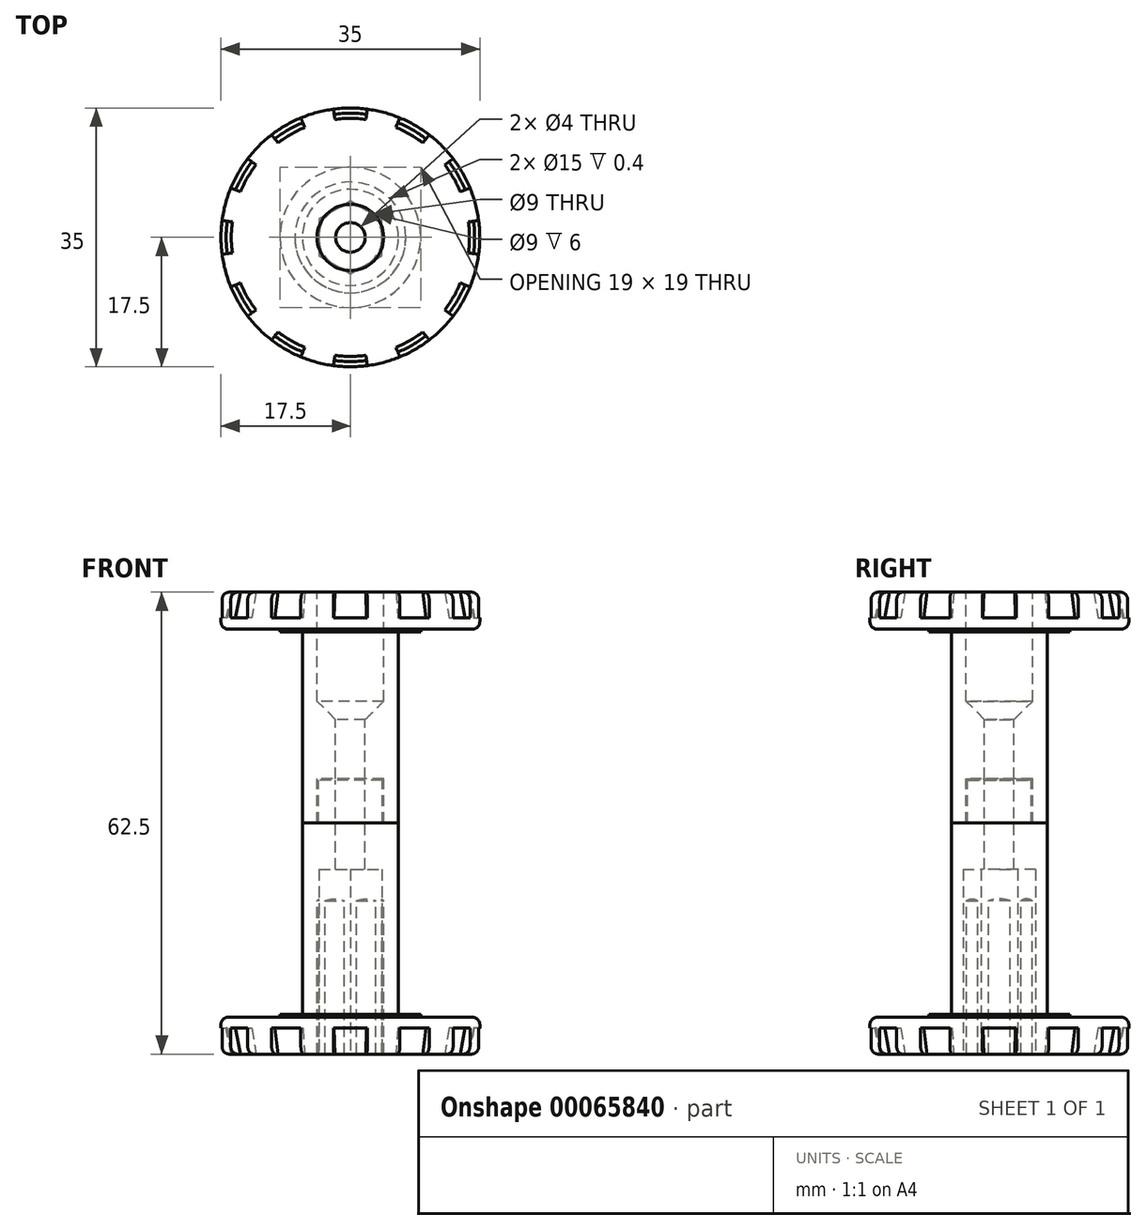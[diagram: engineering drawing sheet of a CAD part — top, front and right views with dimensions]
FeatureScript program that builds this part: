
annotation { "Feature Type Name" : "Feature", "Feature Type Description" : "" }
export const myFeature = defineFeature(function(context is Context, id is Id, definition is map)
    precondition{}
    {
        {
            var Q0;
            Q0=qCreatedBy(makeId("Front.planeOp"),FACE);
            var sketch = newSketch(context, id + "F0", { "sketchPlane" : qUnion([Q0])});
            skLineSegment(sketch, "E0", {"start": v(0, 0) * mm, "end": v(0, -45.3) * mm, "construction": true});
            skLineSegment(sketch, "E1.bottom", {"start": v(4.5, 0) * mm, "end": v(17.5, 0) * mm});
            skLineSegment(sketch, "E1.top", {"start": v(4.5, 62.5) * mm, "end": v(17.5, 62.5) * mm});
            skLineSegment(sketch, "E1.left", {"start": v(4.5, 0) * mm, "end": v(4.5, 62.5) * mm});
            skLineSegment(sketch, "E1.right", {"start": v(17.5, 0) * mm, "end": v(17.5, 62.5) * mm});
            skLineSegment(sketch, "E2", {"start": v(17.5, 5) * mm, "end": v(6.5, 5) * mm});
            skLineSegment(sketch, "E3", {"start": v(6.5, 5) * mm, "end": v(6.5, 31.25) * mm});
            skPoint(sketch, "E4", {"position": v(4.5, 31.25) * mm});
            skLineSegment(sketch, "E5", {"start": v(4.5, 31.25) * mm, "end": v(6.5, 31.25) * mm});
            skLineSegment(sketch, "E6", {"start": v(6.5, 31.25) * mm, "end": v(6.5, 57.5) * mm});
            skLineSegment(sketch, "E7", {"start": v(6.5, 57.5) * mm, "end": v(17.5, 57.5) * mm});
            skLineSegment(sketch, "E8", {"start": v(4.5, 20.75) * mm, "end": v(2, 23.25) * mm});
            skLineSegment(sketch, "E9", {"start": v(2, 23.25) * mm, "end": v(2, 37.25) * mm});
            skLineSegment(sketch, "E10", {"start": v(2, 37.25) * mm, "end": v(4.5, 37.25) * mm});
            skLineSegment(sketch, "E11", {"start": v(2, 37.25) * mm, "end": v(2, 45.25) * mm});
            skLineSegment(sketch, "E12", {"start": v(2, 45.25) * mm, "end": v(4.5, 47.75) * mm});
            skLineSegment(sketch, "E13", {"start": v(4.3, 37.25) * mm, "end": v(4.3, 31.25) * mm});
            skLineSegment(sketch, "E14", {"start": v(4.3, 31.25) * mm, "end": v(4.5, 31.25) * mm});
            skLineSegment(sketch, "E15", {"start": v(4.3, 37.05) * mm, "end": v(2, 37.05) * mm});
            skSolve(sketch);
        }
        {
            var Q0;
            {var subQ4=sQuery(id+"F0.wireOp",EDGE,"E1.bottom");Q0=makeQuery(id+"F0.imprint","IMPRINT",FACE,{"disambiguationData":[TD([[makeQuery(id+"F0.imprint","IMPRINT",EDGE,{"derivedFrom":subQ4}),1.0]])]});}
            var Q1;
            {var subQ1=sQuery(id+"F0.wireOp",EDGE,"E8");Q1=makeQuery(id+"F0.imprint","IMPRINT",FACE,{"disambiguationData":[TD([[makeQuery(id+"F0.imprint","IMPRINT",EDGE,{"derivedFrom":subQ1}),-1.0]])]});}
            var Q2;
            Q2=sQuery(id+"F0.wireOp",EDGE,"E0");
            revolve(context, id + "F1", {"entities" : qUnion([Q0, Q1]), "axis" : qUnion([Q2]), "revolveType" : RevolveType.FULL});
        }
        {
            var Q0;
            {var subQ4=sQuery(id+"F0.wireOp",EDGE,"E1.top");Q0=makeQuery(id+"F0.imprint","IMPRINT",FACE,{"disambiguationData":[TD([[makeQuery(id+"F0.imprint","IMPRINT",EDGE,{"derivedFrom":subQ4}),-1.0]])]});}
            var Q1;
            {var subQ4=sQuery(id+"F0.wireOp",EDGE,"E11");Q1=makeQuery(id+"F0.imprint","IMPRINT",FACE,{"disambiguationData":[TD([[makeQuery(id+"F0.imprint","IMPRINT",EDGE,{"derivedFrom":subQ4}),-1.0]])]});}
            var Q2;
            Q2=sQuery(id+"F0.wireOp",EDGE,"E0");
            revolve(context, id + "F2", {"entities" : qUnion([Q0, Q1]), "axis" : qUnion([Q2]), "revolveType" : RevolveType.FULL});
        }
        {
            var Q0;
            Q0=makeQuery(id+"F1.opRevolve","SWEPT_FACE",FACE,{"disambiguationData":[OSD([sQuery(id+"F0.wireOp",EDGE,"E1.bottom")])]});
            var sketch = newSketch(context, id + "F3", { "sketchPlane" : qUnion([Q0])});
            skCircle(sketch, "E16.cCircle", {"center": v(0, 0) * mm, "radius": 4.25 * mm, "construction": true});
            skLineSegment(sketch, "E16.0", {"start": v(0, 4.9) * mm, "end": v(4.25, 2.45) * mm});
            skLineSegment(sketch, "E16.1", {"start": v(4.25, 2.45) * mm, "end": v(4.25, -2.45) * mm});
            skLineSegment(sketch, "E16.2", {"start": v(4.25, -2.45) * mm, "end": v(0, -4.9) * mm});
            skLineSegment(sketch, "E16.3", {"start": v(0, -4.9) * mm, "end": v(-4.25, -2.45) * mm});
            skLineSegment(sketch, "E16.4", {"start": v(-4.25, -2.45) * mm, "end": v(-4.25, 2.45) * mm});
            skLineSegment(sketch, "E16.5", {"start": v(-4.25, 2.45) * mm, "end": v(0, 4.9) * mm});
            skPoint(sketch, "E16.0.midPoint", {"position": v(2.12, 3.68) * mm});
            skSolve(sketch);
        }
        {
            var Q0;
            {var subQ1=makeQuery(id+"F1.opRevolve","SWEPT_EDGE",EDGE,{"disambiguationData":[OSD([sQuery(id+"F0.wireOp",EDGE,"E1.bottom"),sQuery(id+"F0.wireOp",EDGE,"E1.left")])]});var subQ5=sQuery(id+"F3.wireOp",EDGE,"E16.0");var subQ6=makeQuery(id+"F3.imprint","INTERSECT",VERTEX,{"disambiguationData":[OD(0.0)],"derivedFrom":[subQ1,subQ5]});Q0=makeQuery(id+"F3.imprint","IMPRINT",FACE,{"disambiguationData":[TD([[makeQuery(id+"F3.imprint","IMPRINT",EDGE,{"disambiguationData":[TD([[subQ6,-1.0]])],"derivedFrom":subQ5}),-1.0]])]});}
            var Q1;
            {var subQ0=sQuery(id+"F3.wireOp",EDGE,"E16.5");var subQ1=sQuery(id+"F3.wireOp",EDGE,"E16.4");var subQ2=makeQuery(id+"F3.imprint","INTERSECT",VERTEX,{"derivedFrom":[subQ1,subQ0]});Q1=makeQuery(id+"F3.imprint","IMPRINT",FACE,{"disambiguationData":[TD([[makeQuery(id+"F3.imprint","IMPRINT",EDGE,{"disambiguationData":[TD([[subQ2,1.0]])],"derivedFrom":subQ1}),-1.0]])]});}
            var Q2;
            {var subQ0=sQuery(id+"F3.wireOp",EDGE,"E16.5");var subQ1=sQuery(id+"F3.wireOp",EDGE,"E16.0");var subQ2=makeQuery(id+"F3.imprint","INTERSECT",VERTEX,{"derivedFrom":[subQ1,subQ0]});Q2=makeQuery(id+"F3.imprint","IMPRINT",FACE,{"disambiguationData":[TD([[makeQuery(id+"F3.imprint","IMPRINT",EDGE,{"disambiguationData":[TD([[subQ2,-1.0]])],"derivedFrom":subQ1}),-1.0]])]});}
            var Q3;
            {var subQ0=sQuery(id+"F3.wireOp",EDGE,"E16.1");var subQ1=sQuery(id+"F3.wireOp",EDGE,"E16.0");var subQ2=makeQuery(id+"F3.imprint","INTERSECT",VERTEX,{"derivedFrom":[subQ1,subQ0]});Q3=makeQuery(id+"F3.imprint","IMPRINT",FACE,{"disambiguationData":[TD([[makeQuery(id+"F3.imprint","IMPRINT",EDGE,{"disambiguationData":[TD([[subQ2,1.0]])],"derivedFrom":subQ1}),-1.0]])]});}
            var Q4;
            {var subQ0=sQuery(id+"F3.wireOp",EDGE,"E16.2");var subQ1=sQuery(id+"F3.wireOp",EDGE,"E16.1");var subQ2=makeQuery(id+"F3.imprint","INTERSECT",VERTEX,{"derivedFrom":[subQ1,subQ0]});Q4=makeQuery(id+"F3.imprint","IMPRINT",FACE,{"disambiguationData":[TD([[makeQuery(id+"F3.imprint","IMPRINT",EDGE,{"disambiguationData":[TD([[subQ2,1.0]])],"derivedFrom":subQ1}),-1.0]])]});}
            var Q5;
            {var subQ0=sQuery(id+"F3.wireOp",EDGE,"E16.3");var subQ1=sQuery(id+"F3.wireOp",EDGE,"E16.2");var subQ2=makeQuery(id+"F3.imprint","INTERSECT",VERTEX,{"derivedFrom":[subQ1,subQ0]});Q5=makeQuery(id+"F3.imprint","IMPRINT",FACE,{"disambiguationData":[TD([[makeQuery(id+"F3.imprint","IMPRINT",EDGE,{"disambiguationData":[TD([[subQ2,1.0]])],"derivedFrom":subQ1}),-1.0]])]});}
            var Q6;
            {var subQ0=sQuery(id+"F3.wireOp",EDGE,"E16.4");var subQ1=sQuery(id+"F3.wireOp",EDGE,"E16.3");var subQ2=makeQuery(id+"F3.imprint","INTERSECT",VERTEX,{"derivedFrom":[subQ1,subQ0]});Q6=makeQuery(id+"F3.imprint","IMPRINT",FACE,{"disambiguationData":[TD([[makeQuery(id+"F3.imprint","IMPRINT",EDGE,{"disambiguationData":[TD([[subQ2,1.0]])],"derivedFrom":subQ1}),-1.0]])]});}
            extrude(context, id + "F4", {"entities" : qUnion([Q0, Q1, Q2, Q3, Q4, Q5, Q6]), "operationType" : NewBodyOperationType.REMOVE, "oppositeDirection" : true, "depth" : 25 * mm});
        }
        {
            var Q0;
            Q0=qCreatedBy(makeId("Front.planeOp"),FACE);
            var sketch = newSketch(context, id + "F5", { "sketchPlane" : qUnion([Q0])});
            skLineSegment(sketch, "E17", {"start": v(16.1, 62.5) * mm, "end": v(16.8, 59) * mm});
            skLineSegment(sketch, "E18", {"start": v(17.5, 62.5) * mm, "end": v(17.5, 57.5) * mm});
            skLineSegment(sketch, "E19", {"start": v(16.8, 59) * mm, "end": v(17.5, 59) * mm});
            skLineSegment(sketch, "E20", {"start": v(17.5, 62.5) * mm, "end": v(16.1, 62.5) * mm});
            skLineSegment(sketch, "E21", {"start": v(0, 0) * mm, "end": v(0, -24.57) * mm, "construction": true});
            skSolve(sketch);
        }
        {
            var Q0;
            Q0=makeQuery(id+"F2.opRevolve","SWEPT_EDGE",EDGE,{"disambiguationData":[OSD([sQuery(id+"F0.wireOp",EDGE,"E1.top"),sQuery(id+"F0.wireOp",EDGE,"E1.right")])]});
            var Q1;
            Q1=makeQuery(id+"F1.opRevolve","SWEPT_EDGE",EDGE,{"disambiguationData":[OSD([sQuery(id+"F0.wireOp",EDGE,"E1.bottom"),sQuery(id+"F0.wireOp",EDGE,"E1.right")])]});
            var Q2;
            Q2=makeQuery(id+"F2.opRevolve","SWEPT_EDGE",EDGE,{"disambiguationData":[OSD([sQuery(id+"F0.wireOp",EDGE,"E1.right"),sQuery(id+"F0.wireOp",EDGE,"E7")])]});
            var Q3;
            Q3=makeQuery(id+"F1.opRevolve","SWEPT_EDGE",EDGE,{"disambiguationData":[OSD([sQuery(id+"F0.wireOp",EDGE,"E1.right"),sQuery(id+"F0.wireOp",EDGE,"E2")])]});
            fillet(context, id + "F6", {"entities" : qUnion([Q0, Q1, Q2, Q3]), "radius" : 1 * mm, "tangentPropagation" : true, "allowEdgeOverflow" : false});
        }
        {
            var Q0;
            Q0=makeQuery(id+"F5.imprint","IMPRINT",FACE,{"disambiguationData":[TD([[makeQuery(id+"F5.imprint","IMPRINT",EDGE,{"derivedFrom":sQuery(id+"F5.wireOp",EDGE,"E17")}),1.0]])]});
            var Q1;
            Q1=sQuery(id+"F5.wireOp",EDGE,"E21");
            revolve(context, id + "F7", {"entities" : qUnion([Q0]), "axis" : qUnion([Q1]), "revolveType" : RevolveType.SYMMETRIC, "oppositeDirection" : true, "angle" : 15 * degree});
        }
        {
            var Q0;
            Q0=makeQuery(id+"F7.opRevolve","SWEPT_BODY",BODY,{"disambiguationData":[OSD([sQuery(id+"F5.wireOp",EDGE,"E17"),sQuery(id+"F5.wireOp",EDGE,"E18"),sQuery(id+"F5.wireOp",EDGE,"E19"),sQuery(id+"F5.wireOp",EDGE,"E20")])]});
            var Q1;
            Q1=sQuery(id+"F0.wireOp",EDGE,"E0");
            circularPattern(context, id + "F8", {"operationType" : NewBodyOperationType.REMOVE, "entities" : qUnion([Q0]), "axis" : qUnion([Q1]), "angle" : 360 * degree, "instanceCount" : 12, "equalSpace" : true});
        }
        {
            var Q0;
            Q0=qCreatedBy(makeId("Front.planeOp"),FACE);
            var sketch = newSketch(context, id + "F9", { "sketchPlane" : qUnion([Q0])});
            skLineSegment(sketch, "E22.0", {"start": v(17.5, 0) * mm, "end": v(17.5, 62.5) * mm});
            skLineSegment(sketch, "E23.0", {"start": v(4.5, 0) * mm, "end": v(17.5, 0) * mm});
            skLineSegment(sketch, "E24", {"start": v(17.5, 3.5) * mm, "end": v(16.8, 3.5) * mm});
            skLineSegment(sketch, "E25", {"start": v(16.8, 3.5) * mm, "end": v(16.1, 0) * mm});
            skSolve(sketch);
        }
        {
            var Q0;
            {var subQ3=sQuery(id+"F9.wireOp",EDGE,"E24");Q0=makeQuery(id+"F9.imprint","IMPRINT",FACE,{"disambiguationData":[TD([[makeQuery(id+"F9.imprint","IMPRINT",EDGE,{"derivedFrom":subQ3}),1.0]])]});}
            var Q1;
            Q1=sQuery(id+"F5.wireOp",EDGE,"E21");
            revolve(context, id + "F10", {"entities" : qUnion([Q0]), "axis" : qUnion([Q1]), "revolveType" : RevolveType.SYMMETRIC, "angle" : 15 * degree});
        }
        {
            var Q0;
            Q0=makeQuery(id+"F10.opRevolve","SWEPT_BODY",BODY,{"disambiguationData":[OSD([sQuery(id+"F9.wireOp",EDGE,"E22.0"),sQuery(id+"F9.wireOp",EDGE,"E23.0"),sQuery(id+"F9.wireOp",EDGE,"E24"),sQuery(id+"F9.wireOp",EDGE,"E25")])]});
            var Q1;
            Q1=sQuery(id+"F5.wireOp",EDGE,"E21");
            circularPattern(context, id + "F11", {"operationType" : NewBodyOperationType.REMOVE, "entities" : qUnion([Q0]), "axis" : qUnion([Q1]), "angle" : 360 * degree, "instanceCount" : 12, "equalSpace" : true});
        }
        {
            var Q0;
            Q0=qCreatedBy(makeId("Front.planeOp"),FACE);
            var sketch = newSketch(context, id + "F12", { "sketchPlane" : qUnion([Q0])});
            skLineSegment(sketch, "E26.bottom", {"start": v(7.5, 58.6) * mm, "end": v(9.5, 58.6) * mm});
            skLineSegment(sketch, "E26.top", {"start": v(7.5, 57.1) * mm, "end": v(9.5, 57.1) * mm});
            skLineSegment(sketch, "E26.left", {"start": v(7.5, 58.6) * mm, "end": v(7.5, 57.1) * mm});
            skLineSegment(sketch, "E26.right", {"start": v(9.5, 58.6) * mm, "end": v(9.5, 57.1) * mm});
            skLineSegment(sketch, "E27.bottom", {"start": v(7.5, 5.4) * mm, "end": v(9.5, 5.4) * mm});
            skLineSegment(sketch, "E27.top", {"start": v(7.5, 3.9) * mm, "end": v(9.5, 3.9) * mm});
            skLineSegment(sketch, "E27.left", {"start": v(7.5, 5.4) * mm, "end": v(7.5, 3.9) * mm});
            skLineSegment(sketch, "E27.right", {"start": v(9.5, 5.4) * mm, "end": v(9.5, 3.9) * mm});
            skLineSegment(sketch, "E28", {"start": v(0, 0) * mm, "end": v(0, 11.06) * mm});
            skSolve(sketch);
        }
        {
            var Q0;
            Q0=makeQuery(id+"F12.imprint","IMPRINT",FACE,{"disambiguationData":[TD([[makeQuery(id+"F12.imprint","IMPRINT",EDGE,{"derivedFrom":sQuery(id+"F12.wireOp",EDGE,"E26.bottom")}),-1.0]])]});
            var Q1;
            Q1=sQuery(id+"F12.wireOp",EDGE,"E28");
            revolve(context, id + "F13", {"operationType" : NewBodyOperationType.ADD, "entities" : qUnion([Q0]), "axis" : qUnion([Q1]), "revolveType" : RevolveType.FULL});
        }
        {
            var Q0;
            Q0=makeQuery(id+"F12.imprint","IMPRINT",FACE,{"disambiguationData":[TD([[makeQuery(id+"F12.imprint","IMPRINT",EDGE,{"derivedFrom":sQuery(id+"F12.wireOp",EDGE,"E27.bottom")}),-1.0]])]});
            var Q1;
            Q1=sQuery(id+"F5.wireOp",EDGE,"E21");
            revolve(context, id + "F14", {"operationType" : NewBodyOperationType.ADD, "entities" : qUnion([Q0]), "axis" : qUnion([Q1]), "revolveType" : RevolveType.FULL});
        }
    });
